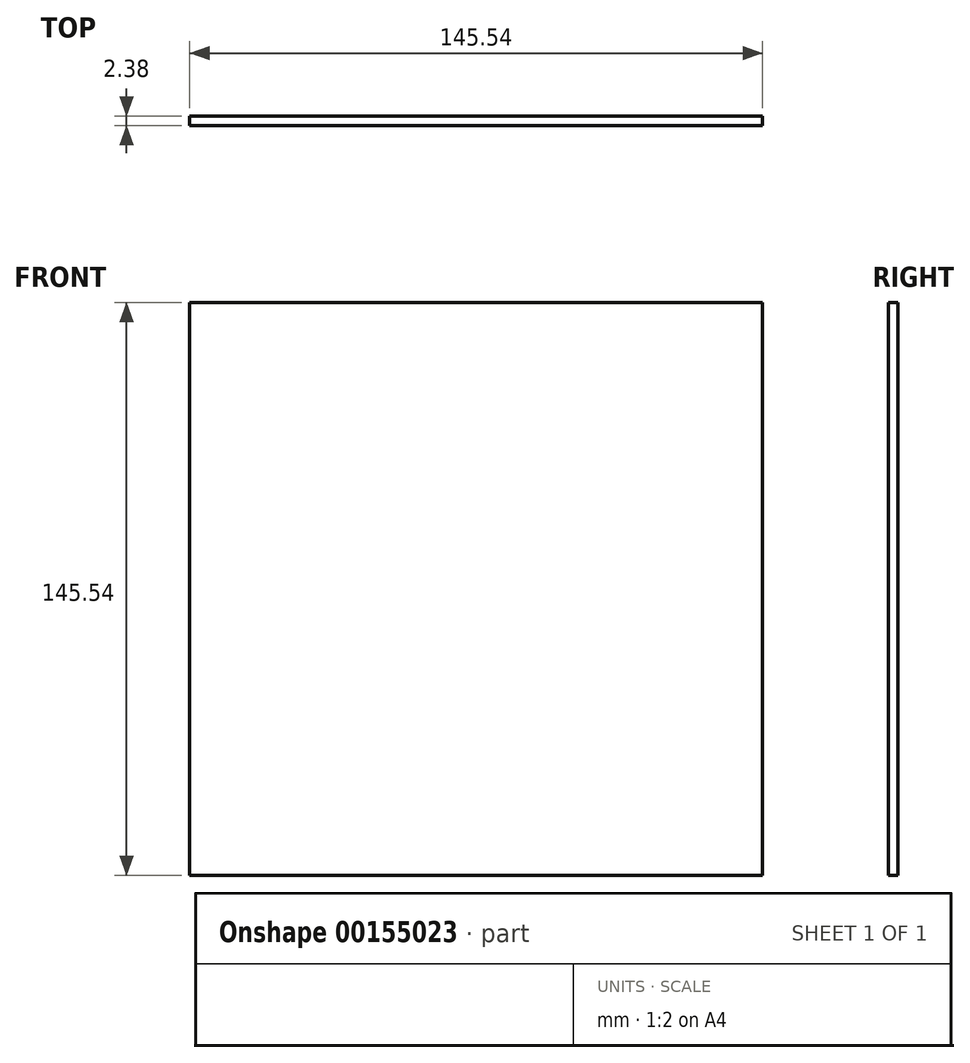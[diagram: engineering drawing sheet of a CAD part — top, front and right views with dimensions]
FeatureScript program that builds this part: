
annotation { "Feature Type Name" : "Feature", "Feature Type Description" : "" }
export const myFeature = defineFeature(function(context is Context, id is Id, definition is map)
    precondition{}
    {
        {
            var Q0;
            Q0=qCreatedBy(makeId("Front.planeOp"),FACE);
            var sketch = newSketch(context, id + "F0", { "sketchPlane" : qUnion([Q0])});
            skLineSegment(sketch, "E0.bottom", {"start": v(-72.77, 72.77) * mm, "end": v(72.77, 72.77) * mm});
            skLineSegment(sketch, "E0.top", {"start": v(-72.77, -72.77) * mm, "end": v(72.77, -72.77) * mm});
            skLineSegment(sketch, "E0.left", {"start": v(-72.77, 72.77) * mm, "end": v(-72.77, -72.77) * mm});
            skLineSegment(sketch, "E0.right", {"start": v(72.77, 72.77) * mm, "end": v(72.77, -72.77) * mm});
            skPoint(sketch, "E0.middle", {"position": v(0, 0) * mm});
            skSolve(sketch);
        }
        {
            var Q0;
            Q0=makeQuery(id+"F0.imprint","IMPRINT",FACE,{"disambiguationData":[TD([[makeQuery(id+"F0.imprint","IMPRINT",EDGE,{"derivedFrom":sQuery(id+"F0.wireOp",EDGE,"E0.bottom")}),-1.0]])]});
            extrude(context, id + "F1", {"entities" : qUnion([Q0]), "depth" : 2.38 * mm});
        }
    });
